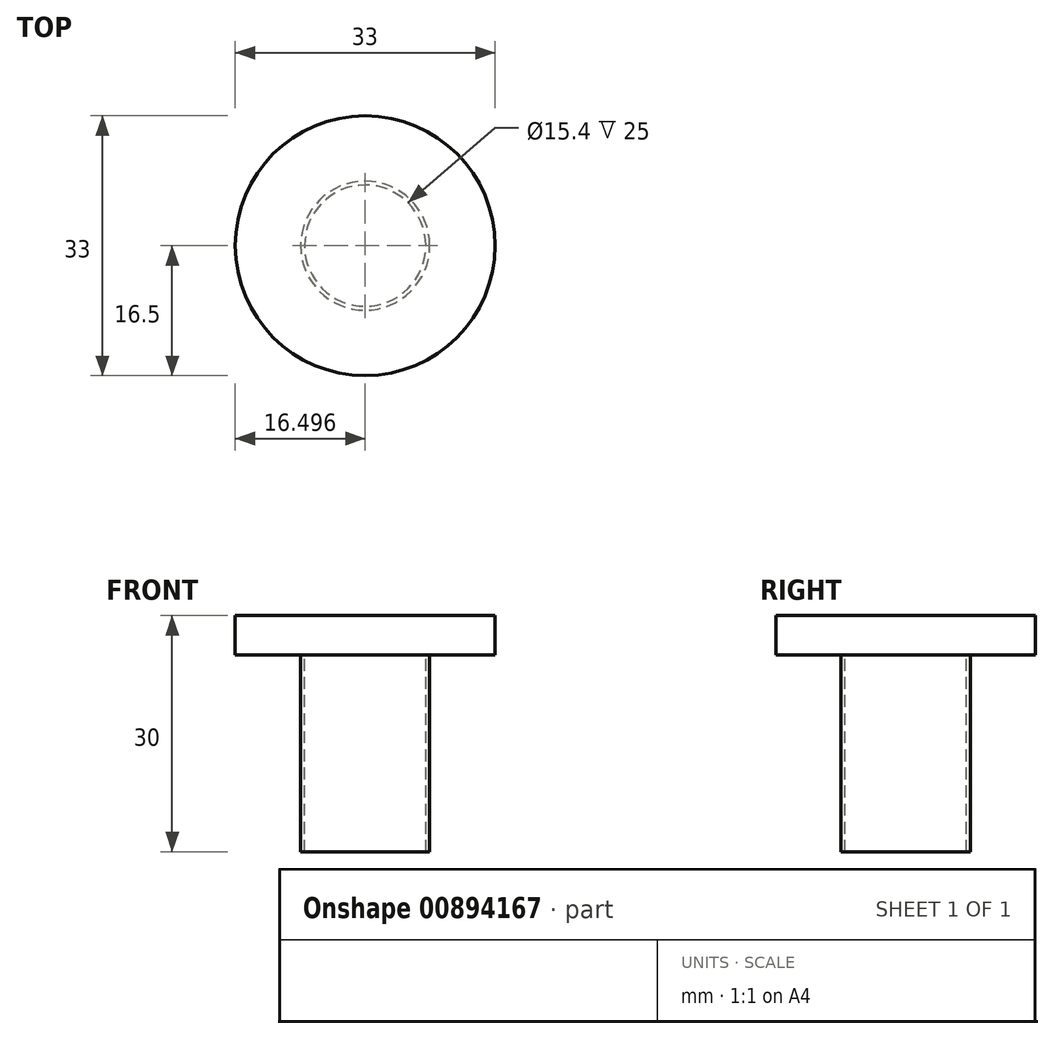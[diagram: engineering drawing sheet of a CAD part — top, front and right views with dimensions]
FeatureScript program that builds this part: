
annotation { "Feature Type Name" : "Feature", "Feature Type Description" : "" }
export const myFeature = defineFeature(function(context is Context, id is Id, definition is map)
    precondition{}
    {
        {
            var Q0;
            Q0=qCreatedBy(makeId("Top.planeOp"),FACE);
            var sketch = newSketch(context, id + "F0", { "sketchPlane" : qUnion([Q0])});
            skCircle(sketch, "E0", {"center": v(-45.86, 17.8) * mm, "radius": 16.5 * mm});
            skCircle(sketch, "E1", {"center": v(-45.86, 17.8) * mm, "radius": 16 * mm});
            skSolve(sketch);
        }
        {
            var Q0;
            Q0=sQuery(id+"F0.wireOp",EDGE,"E1");
            var Q1;
            Q1=sQuery(id+"F0.wireOp",EDGE,"E0");
            extrude(context, id + "F1", {"bodyType" : ToolBodyType.SURFACE, "surfaceEntities" : qUnion([Q0, Q1]), "offsetDistance" : 25 * mm, "depth" : 45 * mm});
        }
        {
            var Q0;
            Q0=qCreatedBy(makeId("Top.planeOp"),FACE);
            var sketch = newSketch(context, id + "F2", { "sketchPlane" : qUnion([Q0])});
            skCircle(sketch, "E2", {"center": v(-45.86, 17.8) * mm, "radius": 16.5 * mm});
            skSolve(sketch);
        }
        {
            var Q0;
            Q0=qSketchRegion(id+"F2",true);
            extrude(context, id + "F3", {"entities" : qUnion([Q0]), "depth" : 5 * mm});
        }
        {
            var Q0;
            Q0=qCreatedBy(makeId("Top.planeOp"),FACE);
            var sketch = newSketch(context, id + "F4", { "sketchPlane" : qUnion([Q0])});
            skCircle(sketch, "E3", {"center": v(-45.86, 17.8) * mm, "radius": 7.7 * mm});
            skCircle(sketch, "E4", {"center": v(-45.86, 17.8) * mm, "radius": 8.2 * mm});
            skSolve(sketch);
        }
        {
            var Q0;
            Q0 = qSketchRegion(id + "F4", true);
            extrude(context, id + "F5", {"entities" : qUnion([Q0]), "operationType" : NewBodyOperationType.ADD, "oppositeDirection" : true, "depth" : 25 * mm, "offsetDistance" : 25 * mm});
        }
    });
